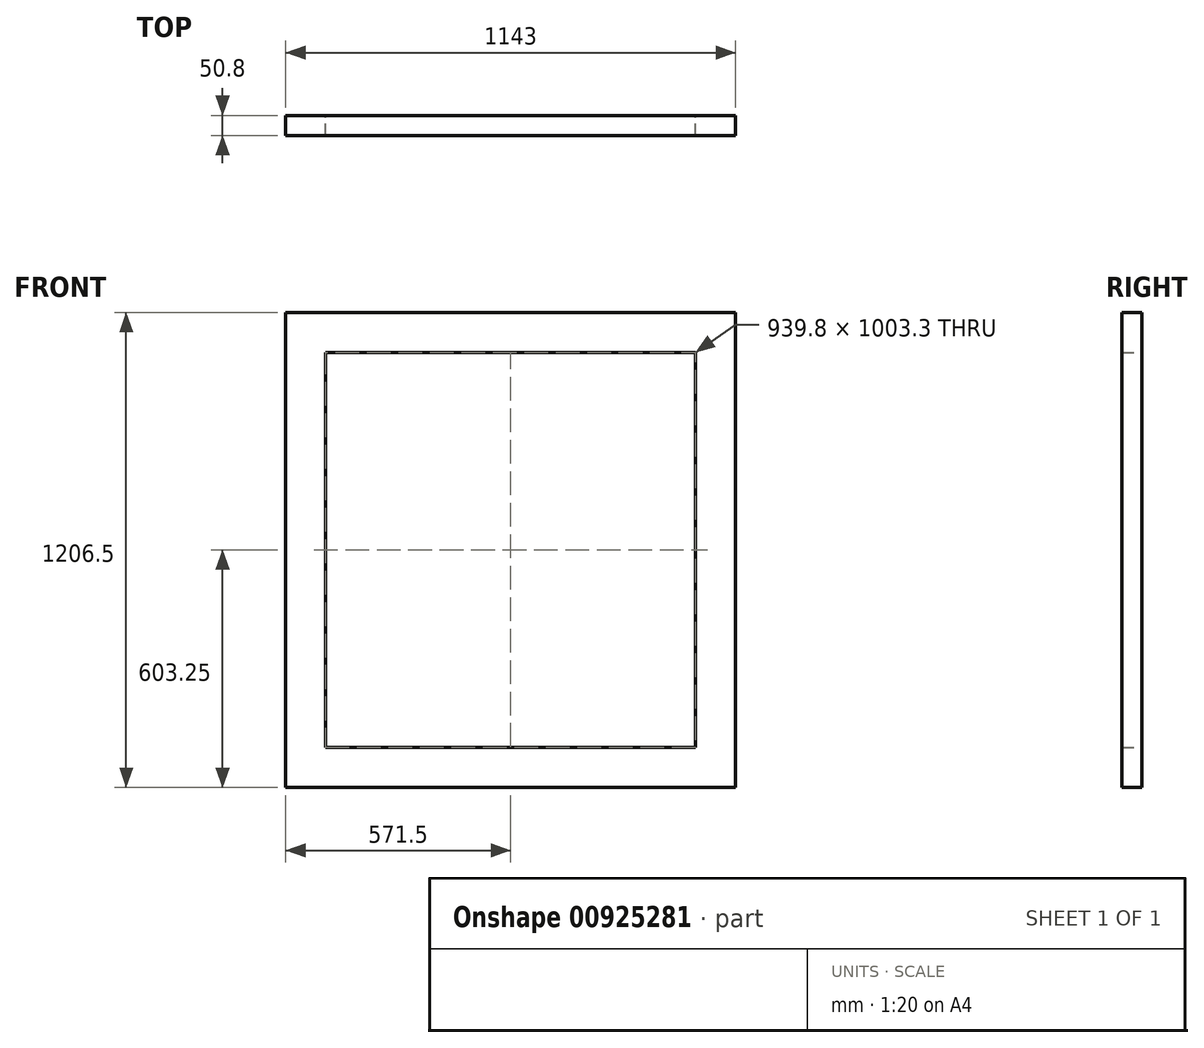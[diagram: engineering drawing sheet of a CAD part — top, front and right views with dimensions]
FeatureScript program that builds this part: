
annotation { "Feature Type Name" : "Feature", "Feature Type Description" : "" }
export const myFeature = defineFeature(function(context is Context, id is Id, definition is map)
    precondition{}
    {
        {
            var Q0;
            Q0=qCreatedBy(makeId("Front.planeOp"),FACE);
            var sketch = newSketch(context, id + "F0", { "sketchPlane" : qUnion([Q0])});
            skLineSegment(sketch, "E0.bottom", {"start": v(0, 0) * mm, "end": v(1143, 0) * mm});
            skLineSegment(sketch, "E0.top", {"start": v(0, 1206.5) * mm, "end": v(1143, 1206.5) * mm});
            skLineSegment(sketch, "E0.left", {"start": v(0, 0) * mm, "end": v(0, 1206.5) * mm});
            skLineSegment(sketch, "E0.right", {"start": v(1143, 0) * mm, "end": v(1143, 1206.5) * mm});
            skLineSegment(sketch, "E1.bottom", {"start": v(101.6, 1104.9) * mm, "end": v(1041.4, 1104.9) * mm});
            skLineSegment(sketch, "E1.top", {"start": v(101.6, 101.6) * mm, "end": v(1041.4, 101.6) * mm});
            skLineSegment(sketch, "E1.left", {"start": v(101.6, 1104.9) * mm, "end": v(101.6, 101.6) * mm});
            skLineSegment(sketch, "E1.right", {"start": v(1041.4, 1104.9) * mm, "end": v(1041.4, 101.6) * mm});
            skSolve(sketch);
        }
        {
            var Q0;
            Q0=makeQuery(id+"F0.imprint","IMPRINT",FACE,{"disambiguationData":[TD([[makeQuery(id+"F0.imprint","IMPRINT",EDGE,{"derivedFrom":sQuery(id+"F0.wireOp",EDGE,"E0.bottom")}),1.0]])]});
            extrude(context, id + "F1", {"entities" : qUnion([Q0]), "depth" : 50.8 * mm, "offsetDistance" : 25.4 * mm});
        }
    });
